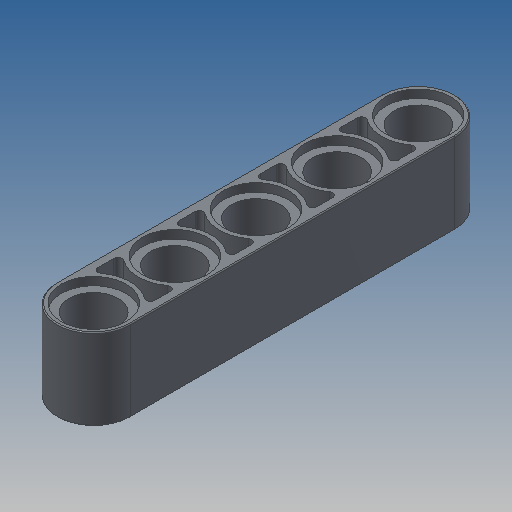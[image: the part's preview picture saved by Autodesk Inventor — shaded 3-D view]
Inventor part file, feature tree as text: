
AUTODESK INVENTOR PART (.ipt)
format: ipt  version: 2022.2 (Build 262287000, 287)  size: 297,472 bytes
history: native  units: mm
features: extrude x3, sketch x2, mirror x1, fillet x1
ambient origin geometry x8: Origin, YZ Plane, XZ Plane, XY Plane, X Axis, Y Axis, Z Axis, Center Point
bodies: Solid1 (feature_tree)
feature tree (7):
  extrude  "Extrusion1"  Depth=6.4mm
  sketch  "Sketch6"  dims[d14=8.0mm d15=0.0mm d32=7.2mm d34=8.0mm d36=0.8mm d41=0.8mm d42=0.0mm d43=3.1mm d44=0.0mm d46=0.4mm d47=0.1mm]
  extrude  "Extrusion7"  Depth=7.2mm
  extrude  "Extrusion8"  Depth=8.0mm
  mirror  "Mirror1"
  fillet  "Fillet1"  Radius=0.8mm
  sketch  "Sketch1"  dims[d8=4.8mm d9=6.4mm]
